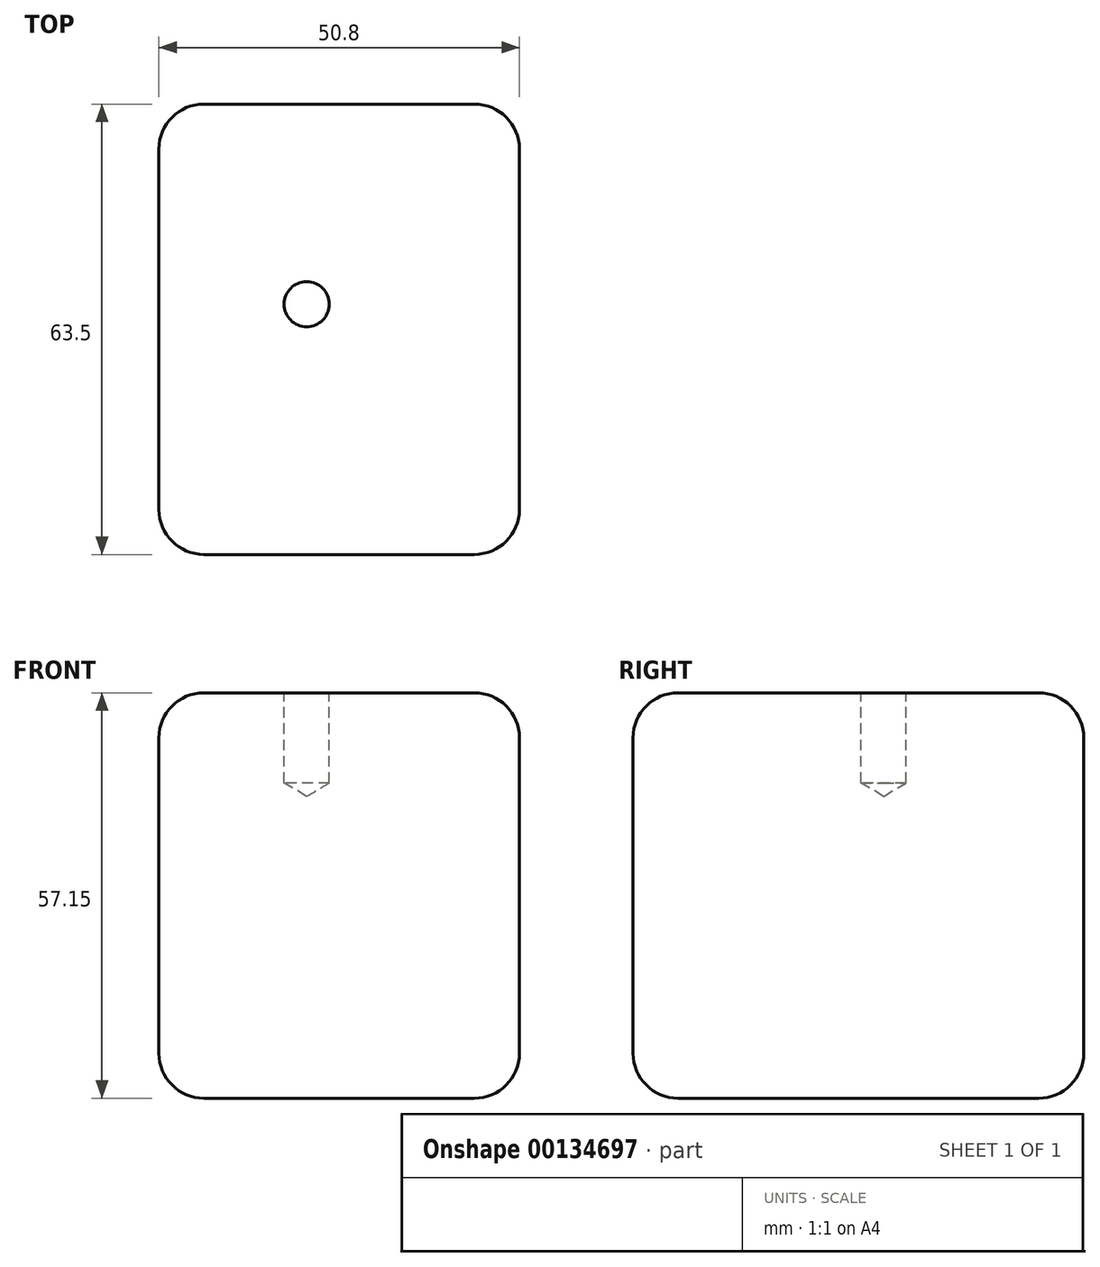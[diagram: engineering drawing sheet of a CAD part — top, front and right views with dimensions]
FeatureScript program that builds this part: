
annotation { "Feature Type Name" : "Feature", "Feature Type Description" : "" }
export const myFeature = defineFeature(function(context is Context, id is Id, definition is map)
    precondition{}
    {
        {
            var Q0;
            Q0=qCreatedBy(makeId("Front.planeOp"),FACE);
            var sketch = newSketch(context, id + "F0", { "sketchPlane" : qUnion([Q0])});
            skLineSegment(sketch, "E0", {"start": v(0, 0) * mm, "end": v(50.8, 0) * mm});
            skLineSegment(sketch, "E1", {"start": v(50.8, 0) * mm, "end": v(50.8, 57.15) * mm});
            skLineSegment(sketch, "E2", {"start": v(0, 0) * mm, "end": v(0, 57.15) * mm});
            skLineSegment(sketch, "E3", {"start": v(0, 57.15) * mm, "end": v(50.8, 57.15) * mm});
            skSolve(sketch);
        }
        {
            var Q0;
            Q0 = qSketchRegion(id + "F0", true);
            extrude(context, id + "F1", {"entities" : qUnion([Q0]), "depth" : 63.5 * mm});
        }
        {
            var Q0;
            Q0=makeQuery(id+"F1.opExtrude","SWEPT_FACE",FACE,{"disambiguationData":[OSD([sQuery(id+"F0.wireOp",EDGE,"E3")])]});
            var sketch = newSketch(context, id + "F2", { "sketchPlane" : qUnion([Q0])});
            skPoint(sketch, "E4", {"position": v(20.82, -28.22) * mm});
            skSolve(sketch);
        }
        {
            var Q0;
            Q0=sQuery(id+"F2.wireOp",VERTEX,"E4");
            var Q1;
            Q1=makeQuery(id+"F1.opExtrude","SWEPT_BODY",BODY,{"disambiguationData":[OSD([sQuery(id+"F0.wireOp",EDGE,"E0"),sQuery(id+"F0.wireOp",EDGE,"E1"),sQuery(id+"F0.wireOp",EDGE,"E2"),sQuery(id+"F0.wireOp",EDGE,"E3")])]});
            hole(context, id + "F3", {"style" : HoleStyle.SIMPLE, "endStyle" : HoleEndStyle.BLIND, "holeDiameter" : 6.35 * mm, "holeDepth" : 12.7 * mm, "startFromSketch" : true, "locations" : qUnion([Q0]), "scope" : qUnion([Q1])});
        }
        {
            var Q0;
            Q0=makeQuery(id+"F1.opExtrude","SWEPT_FACE",FACE,{"disambiguationData":[OSD([sQuery(id+"F0.wireOp",EDGE,"E1")])]});
            var Q1;
            Q1=makeQuery(id+"F1.opExtrude","CAP_FACE",FACE,{"disambiguationData":[OSD([sQuery(id+"F0.wireOp",EDGE,"E0"),sQuery(id+"F0.wireOp",EDGE,"E1"),sQuery(id+"F0.wireOp",EDGE,"E2"),sQuery(id+"F0.wireOp",EDGE,"E3")])],"isStart":false});
            var Q2;
            Q2=makeQuery(id+"F1.opExtrude","CAP_EDGE",EDGE,{"disambiguationData":[OSD([sQuery(id+"F0.wireOp",EDGE,"E3")])],"isStart":true});
            var Q3;
            Q3=makeQuery(id+"F1.opExtrude","SWEPT_EDGE",EDGE,{"disambiguationData":[OSD([sQuery(id+"F0.wireOp",EDGE,"E2"),sQuery(id+"F0.wireOp",EDGE,"E3")])]});
            var Q4;
            Q4=makeQuery(id+"F1.opExtrude","CAP_FACE",FACE,{"disambiguationData":[OSD([sQuery(id+"F0.wireOp",EDGE,"E0"),sQuery(id+"F0.wireOp",EDGE,"E1"),sQuery(id+"F0.wireOp",EDGE,"E2"),sQuery(id+"F0.wireOp",EDGE,"E3")])],"isStart":true});
            var Q5;
            Q5=makeQuery(id+"F1.opExtrude","SWEPT_FACE",FACE,{"disambiguationData":[OSD([sQuery(id+"F0.wireOp",EDGE,"E2")])]});
            fillet(context, id + "F4", {"entities" : qUnion([Q0, Q1, Q2, Q3, Q4, Q5]), "radius" : 6.35 * mm, "tangentPropagation" : true, "allowEdgeOverflow" : false});
        }
    });
